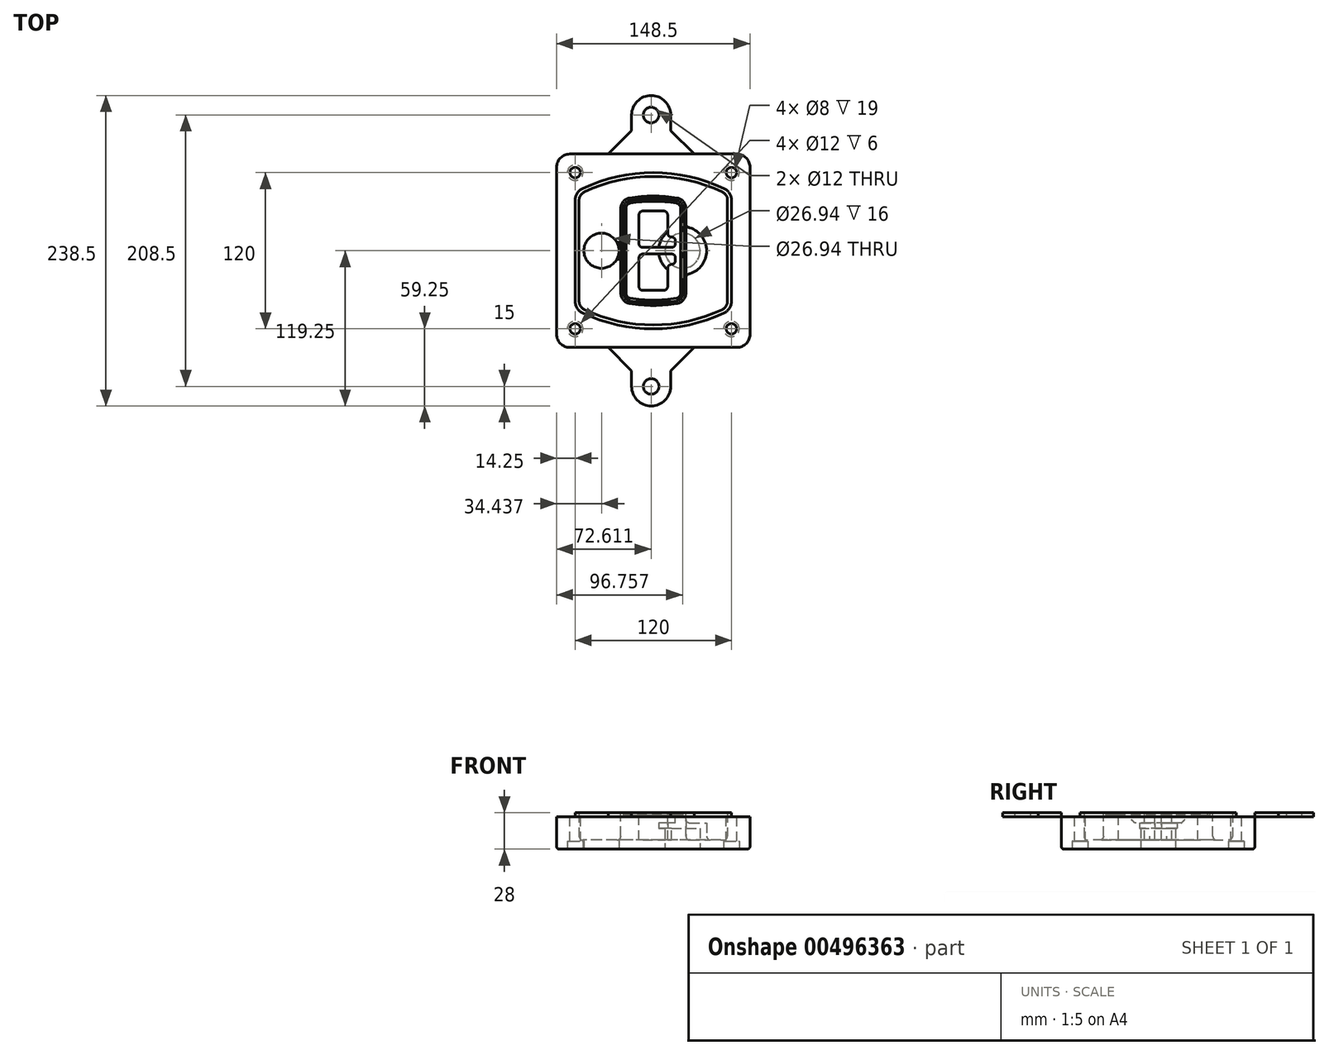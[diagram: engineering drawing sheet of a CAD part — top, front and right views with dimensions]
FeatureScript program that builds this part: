
annotation { "Feature Type Name" : "Feature", "Feature Type Description" : "" }
export const myFeature = defineFeature(function(context is Context, id is Id, definition is map)
    precondition{}
    {
        {
            var Q0;
            Q0=qCreatedBy(makeId("Top.planeOp"),FACE);
            var sketch = newSketch(context, id + "F0", { "sketchPlane" : qUnion([Q0])});
            skPoint(sketch, "E0.rect.middle", {"position": v(0, 0) * mm});
            skLineSegment(sketch, "E1.bottom", {"start": v(-64.25, -74.25) * mm, "end": v(64.25, -74.25) * mm});
            skLineSegment(sketch, "E1.top", {"start": v(-64.25, 74.25) * mm, "end": v(64.25, 74.25) * mm});
            skLineSegment(sketch, "E1.left", {"start": v(-74.25, -64.25) * mm, "end": v(-74.25, 64.25) * mm});
            skLineSegment(sketch, "E1.right", {"start": v(74.25, -64.25) * mm, "end": v(74.25, 64.25) * mm});
            skLineSegment(sketch, "E2", {"start": v(-74.25, 74.25) * mm, "end": v(74.25, -74.25) * mm, "construction": true});
            skLineSegment(sketch, "E3", {"start": v(74.25, 74.25) * mm, "end": v(-74.25, -74.25) * mm, "construction": true});
            skCircle(sketch, "E4", {"center": v(-60, 60) * mm, "radius": 4 * mm});
            skCircle(sketch, "E5", {"center": v(60, 60) * mm, "radius": 4 * mm});
            skCircle(sketch, "E6", {"center": v(60, -60) * mm, "radius": 4 * mm});
            skCircle(sketch, "E7", {"center": v(-60, -60) * mm, "radius": 4 * mm});
            skLineSegment(sketch, "E8", {"start": v(-60, 60) * mm, "end": v(60, 60) * mm, "construction": true});
            skLineSegment(sketch, "E9", {"start": v(60, 60) * mm, "end": v(60, -60) * mm, "construction": true});
            skLineSegment(sketch, "E10", {"start": v(60, -60) * mm, "end": v(-60, -60) * mm, "construction": true});
            skLineSegment(sketch, "E11", {"start": v(-60, -60) * mm, "end": v(-60, 60) * mm, "construction": true});
            skLineSegment(sketch, "E12", {"start": v(-60, 38.83) * mm, "end": v(-60, -38.83) * mm});
            skLineSegment(sketch, "E13", {"start": v(60, 38.83) * mm, "end": v(60, -38.83) * mm});
            skArc(sketch, "E14", {"start": v(54.26, 47.88) * mm, "mid": v(0, 60) * mm, "end": v(-54.26, 47.88) * mm});
            skArc(sketch, "E15", {"start": v(-54.26, -47.88) * mm, "mid": v(0, -60) * mm, "end": v(54.26, -47.88) * mm});
            skLineSegment(sketch, "E16", {"start": v(-60, 0) * mm, "end": v(60, 0) * mm, "construction": true});
            skPoint(sketch, "E17.visualSharp", {"position": v(-60, -45) * mm});
            skArc(sketch, "E17.filletArc", {"start": v(-60, -38.83) * mm, "mid": v(-58.44, -44.2) * mm, "end": v(-54.26, -47.88) * mm});
            skPoint(sketch, "E18.visualSharp", {"position": v(-60, 45) * mm});
            skArc(sketch, "E18.filletArc", {"start": v(-54.26, 47.88) * mm, "mid": v(-58.44, 44.2) * mm, "end": v(-60, 38.83) * mm});
            skPoint(sketch, "E19.visualSharp", {"position": v(60, 45) * mm});
            skArc(sketch, "E19.filletArc", {"start": v(60, 38.83) * mm, "mid": v(58.44, 44.2) * mm, "end": v(54.26, 47.88) * mm});
            skPoint(sketch, "E20.visualSharp", {"position": v(60, -45) * mm});
            skArc(sketch, "E20.filletArc", {"start": v(54.26, -47.88) * mm, "mid": v(58.44, -44.2) * mm, "end": v(60, -38.83) * mm});
            skPoint(sketch, "E21.visualSharp", {"position": v(-74.25, 74.25) * mm});
            skArc(sketch, "E21.filletArc", {"start": v(-64.25, 74.25) * mm, "mid": v(-71.32, 71.32) * mm, "end": v(-74.25, 64.25) * mm});
            skPoint(sketch, "E22.visualSharp", {"position": v(74.25, 74.25) * mm});
            skArc(sketch, "E22.filletArc", {"start": v(74.25, 64.25) * mm, "mid": v(71.32, 71.32) * mm, "end": v(64.25, 74.25) * mm});
            skPoint(sketch, "E23.visualSharp", {"position": v(74.25, -74.25) * mm});
            skArc(sketch, "E23.filletArc", {"start": v(64.25, -74.25) * mm, "mid": v(71.32, -71.32) * mm, "end": v(74.25, -64.25) * mm});
            skPoint(sketch, "E24.visualSharp", {"position": v(-74.25, -74.25) * mm});
            skArc(sketch, "E24.filletArc", {"start": v(-74.25, -64.25) * mm, "mid": v(-71.32, -71.32) * mm, "end": v(-64.25, -74.25) * mm});
            skArc(sketch, "E25.0", {"start": v(57, 38.83) * mm, "mid": v(55.9, 42.58) * mm, "end": v(52.98, 45.17) * mm});
            skLineSegment(sketch, "E25.1", {"start": v(57, 38.83) * mm, "end": v(57, -38.83) * mm});
            skArc(sketch, "E25.2", {"start": v(52.98, -45.17) * mm, "mid": v(55.9, -42.58) * mm, "end": v(57, -38.83) * mm});
            skArc(sketch, "E25.3", {"start": v(-52.98, -45.17) * mm, "mid": v(0, -57) * mm, "end": v(52.98, -45.17) * mm});
            skArc(sketch, "E25.4", {"start": v(-57, -38.83) * mm, "mid": v(-55.9, -42.58) * mm, "end": v(-52.98, -45.17) * mm});
            skArc(sketch, "E25.5", {"start": v(52.98, 45.17) * mm, "mid": v(0, 57) * mm, "end": v(-52.98, 45.17) * mm});
            skLineSegment(sketch, "E25.6", {"start": v(-57, 38.83) * mm, "end": v(-57, -38.83) * mm});
            skArc(sketch, "E25.7", {"start": v(-52.98, 45.17) * mm, "mid": v(-55.9, 42.58) * mm, "end": v(-57, 38.83) * mm});
            skArc(sketch, "E26.0", {"start": v(-55.96, 51.5) * mm, "mid": v(-61.82, 46.33) * mm, "end": v(-64, 38.83) * mm});
            skArc(sketch, "E26.1", {"start": v(55.96, 51.5) * mm, "mid": v(0, 64) * mm, "end": v(-55.96, 51.5) * mm});
            skArc(sketch, "E26.2", {"start": v(64, 38.83) * mm, "mid": v(61.82, 46.33) * mm, "end": v(55.96, 51.5) * mm});
            skLineSegment(sketch, "E26.3", {"start": v(64, 38.83) * mm, "end": v(64, -38.83) * mm});
            skArc(sketch, "E26.4", {"start": v(55.96, -51.5) * mm, "mid": v(61.82, -46.33) * mm, "end": v(64, -38.83) * mm});
            skLineSegment(sketch, "E26.5", {"start": v(-64, 38.83) * mm, "end": v(-64, -38.83) * mm});
            skArc(sketch, "E26.6", {"start": v(-55.96, -51.5) * mm, "mid": v(0, -64) * mm, "end": v(55.96, -51.5) * mm});
            skArc(sketch, "E26.7", {"start": v(-64, -38.83) * mm, "mid": v(-61.82, -46.33) * mm, "end": v(-55.96, -51.5) * mm});
            skSolve(sketch);
        }
        {
            var Q0;
            Q0=makeQuery(id+"F0.imprint","IMPRINT",FACE,{"disambiguationData":[TD([[makeQuery(id+"F0.imprint","IMPRINT",EDGE,{"derivedFrom":sQuery(id+"F0.wireOp",EDGE,"E1.bottom")}),1.0]])]});
            var Q1;
            Q1=makeQuery(id+"F0.imprint","IMPRINT",FACE,{"disambiguationData":[TD([[makeQuery(id+"F0.imprint","IMPRINT",EDGE,{"derivedFrom":sQuery(id+"F0.wireOp",EDGE,"E12")}),1.0]])]});
            var Q2;
            Q2=makeQuery(id+"F0.imprint","IMPRINT",FACE,{"disambiguationData":[TD([[makeQuery(id+"F0.imprint","IMPRINT",EDGE,{"derivedFrom":sQuery(id+"F0.wireOp",EDGE,"E25.0")}),1.0]])]});
            var Q3;
            Q3=makeQuery(id+"F0.imprint","IMPRINT",FACE,{"disambiguationData":[TD([[makeQuery(id+"F0.imprint","IMPRINT",EDGE,{"derivedFrom":sQuery(id+"F0.wireOp",EDGE,"E12")}),-1.0]])]});
            extrude(context, id + "F1", {"entities" : qUnion([Q0, Q1, Q2, Q3]), "oppositeDirection" : true, "depth" : 25 * mm});
        }
        {
            var Q0;
            Q0=makeQuery(id+"F0.imprint","IMPRINT",FACE,{"disambiguationData":[TD([[makeQuery(id+"F0.imprint","IMPRINT",EDGE,{"derivedFrom":sQuery(id+"F0.wireOp",EDGE,"E12")}),1.0]])]});
            extrude(context, id + "F2", {"entities" : qUnion([Q0]), "operationType" : NewBodyOperationType.ADD, "depth" : 3 * mm});
        }
        {
            var Q0;
            Q0=makeQuery(id+"F0.imprint","IMPRINT",FACE,{"disambiguationData":[TD([[makeQuery(id+"F0.imprint","IMPRINT",EDGE,{"derivedFrom":sQuery(id+"F0.wireOp",EDGE,"E25.0")}),1.0]])]});
            extrude(context, id + "F3", {"entities" : qUnion([Q0]), "operationType" : NewBodyOperationType.REMOVE, "oppositeDirection" : true, "depth" : 18 * mm});
        }
        {
            var Q0;
            Q0=makeQuery(id+"F2.opExtrude","CAP_FACE",FACE,{"disambiguationData":[OSD([sQuery(id+"F0.wireOp",EDGE,"E12"),sQuery(id+"F0.wireOp",EDGE,"E13"),sQuery(id+"F0.wireOp",EDGE,"E14"),sQuery(id+"F0.wireOp",EDGE,"E15"),sQuery(id+"F0.wireOp",EDGE,"E17.filletArc"),sQuery(id+"F0.wireOp",EDGE,"E18.filletArc"),sQuery(id+"F0.wireOp",EDGE,"E19.filletArc"),sQuery(id+"F0.wireOp",EDGE,"E20.filletArc"),sQuery(id+"F0.wireOp",EDGE,"E25.0"),sQuery(id+"F0.wireOp",EDGE,"E25.1"),sQuery(id+"F0.wireOp",EDGE,"E25.2"),sQuery(id+"F0.wireOp",EDGE,"E25.3"),sQuery(id+"F0.wireOp",EDGE,"E25.4"),sQuery(id+"F0.wireOp",EDGE,"E25.5"),sQuery(id+"F0.wireOp",EDGE,"E25.6"),sQuery(id+"F0.wireOp",EDGE,"E25.7")])],"isStart":false});
            var sketch = newSketch(context, id + "F4", { "sketchPlane" : qUnion([Q0])});
            skArc(sketch, "E27.0", {"start": v(-18.34, -40.45) * mm, "mid": v(0, -42) * mm, "end": v(18.34, -40.45) * mm});
            skArc(sketch, "E28.0", {"start": v(18.34, 40.45) * mm, "mid": v(0, 42) * mm, "end": v(-18.34, 40.45) * mm});
            skLineSegment(sketch, "E29", {"start": v(-25, 32.57) * mm, "end": v(-25, -32.57) * mm});
            skLineSegment(sketch, "E30", {"start": v(25, 32.57) * mm, "end": v(25, -32.57) * mm});
            skLineSegment(sketch, "E31", {"start": v(-25, 39.1) * mm, "end": v(25, 39.1) * mm, "construction": true});
            skLineSegment(sketch, "E32", {"start": v(-25, -39.1) * mm, "end": v(25, -39.1) * mm, "construction": true});
            skPoint(sketch, "E33.visualSharp", {"position": v(-25, 39.1) * mm});
            skArc(sketch, "E33.filletArc", {"start": v(-18.34, 40.45) * mm, "mid": v(-23.11, 37.73) * mm, "end": v(-25, 32.57) * mm});
            skPoint(sketch, "E34.visualSharp", {"position": v(25, 39.1) * mm});
            skArc(sketch, "E34.filletArc", {"start": v(25, 32.57) * mm, "mid": v(23.11, 37.73) * mm, "end": v(18.34, 40.45) * mm});
            skPoint(sketch, "E35.visualSharp", {"position": v(25, -39.1) * mm});
            skArc(sketch, "E35.filletArc", {"start": v(18.34, -40.45) * mm, "mid": v(23.11, -37.73) * mm, "end": v(25, -32.57) * mm});
            skPoint(sketch, "E36.visualSharp", {"position": v(-25, -39.1) * mm});
            skArc(sketch, "E36.filletArc", {"start": v(-25, -32.57) * mm, "mid": v(-23.11, -37.73) * mm, "end": v(-18.34, -40.45) * mm});
            skArc(sketch, "E37.0", {"start": v(52.98, 45.17) * mm, "mid": v(0, 57) * mm, "end": v(-52.98, 45.17) * mm});
            skArc(sketch, "E37.1", {"start": v(-52.98, 45.17) * mm, "mid": v(-55.9, 42.58) * mm, "end": v(-57, 38.83) * mm});
            skLineSegment(sketch, "E37.2", {"start": v(-57, 38.83) * mm, "end": v(-57, -38.83) * mm});
            skArc(sketch, "E37.3", {"start": v(-57, -38.83) * mm, "mid": v(-55.9, -42.58) * mm, "end": v(-52.98, -45.17) * mm});
            skArc(sketch, "E37.4", {"start": v(-52.98, -45.17) * mm, "mid": v(0, -57) * mm, "end": v(52.98, -45.17) * mm});
            skArc(sketch, "E37.5", {"start": v(52.98, -45.17) * mm, "mid": v(55.9, -42.58) * mm, "end": v(57, -38.83) * mm});
            skLineSegment(sketch, "E37.6", {"start": v(57, 38.83) * mm, "end": v(57, -38.83) * mm});
            skArc(sketch, "E37.7", {"start": v(57, 38.83) * mm, "mid": v(55.9, 42.58) * mm, "end": v(52.98, 45.17) * mm});
            skLineSegment(sketch, "E38.0", {"start": v(23, 32.57) * mm, "end": v(23, -32.57) * mm});
            skArc(sketch, "E38.1", {"start": v(18, -38.48) * mm, "mid": v(21.58, -36.44) * mm, "end": v(23, -32.57) * mm});
            skArc(sketch, "E38.2", {"start": v(-18, -38.48) * mm, "mid": v(0, -40) * mm, "end": v(18, -38.48) * mm});
            skArc(sketch, "E38.3", {"start": v(-23, -32.57) * mm, "mid": v(-21.58, -36.44) * mm, "end": v(-18, -38.48) * mm});
            skLineSegment(sketch, "E38.4", {"start": v(-23, 32.57) * mm, "end": v(-23, -32.57) * mm});
            skArc(sketch, "E38.5", {"start": v(23, 32.57) * mm, "mid": v(21.58, 36.44) * mm, "end": v(18, 38.48) * mm});
            skArc(sketch, "E38.6", {"start": v(-18, 38.48) * mm, "mid": v(-21.58, 36.44) * mm, "end": v(-23, 32.57) * mm});
            skArc(sketch, "E38.7", {"start": v(18, 38.48) * mm, "mid": v(0, 40) * mm, "end": v(-18, 38.48) * mm});
            skArc(sketch, "E39.0", {"start": v(21, 32.57) * mm, "mid": v(20.06, 35.15) * mm, "end": v(17.67, 36.5) * mm});
            skLineSegment(sketch, "E39.1", {"start": v(21, 32.57) * mm, "end": v(21, -32.57) * mm});
            skArc(sketch, "E39.2", {"start": v(17.67, -36.5) * mm, "mid": v(20.06, -35.15) * mm, "end": v(21, -32.57) * mm});
            skArc(sketch, "E39.3", {"start": v(-17.67, -36.5) * mm, "mid": v(0, -38) * mm, "end": v(17.67, -36.5) * mm});
            skArc(sketch, "E39.4", {"start": v(-21, -32.57) * mm, "mid": v(-20.06, -35.15) * mm, "end": v(-17.67, -36.5) * mm});
            skArc(sketch, "E39.5", {"start": v(17.67, 36.5) * mm, "mid": v(0, 38) * mm, "end": v(-17.67, 36.5) * mm});
            skLineSegment(sketch, "E39.6", {"start": v(-21, 32.57) * mm, "end": v(-21, -32.57) * mm});
            skArc(sketch, "E39.7", {"start": v(-17.67, 36.5) * mm, "mid": v(-20.06, 35.15) * mm, "end": v(-21, 32.57) * mm});
            skLineSegment(sketch, "E40", {"start": v(-25, 0) * mm, "end": v(25, 0) * mm, "construction": true});
            skLineSegment(sketch, "E41", {"start": v(-11, 5.5) * mm, "end": v(-11, 27.5) * mm});
            skLineSegment(sketch, "E42", {"start": v(-8, 30.5) * mm, "end": v(8, 30.5) * mm});
            skLineSegment(sketch, "E43", {"start": v(11, 27.5) * mm, "end": v(11, 13.5) * mm});
            skLineSegment(sketch, "E44", {"start": v(14, 10.5) * mm, "end": v(14, 10.5) * mm});
            skLineSegment(sketch, "E45", {"start": v(17, 7.5) * mm, "end": v(17, 5.5) * mm});
            skLineSegment(sketch, "E46", {"start": v(14, 2.5) * mm, "end": v(-8, 2.5) * mm});
            skPoint(sketch, "E47.visualSharp", {"position": v(-11, 30.5) * mm});
            skArc(sketch, "E47.filletArc", {"start": v(-8, 30.5) * mm, "mid": v(-10.12, 29.62) * mm, "end": v(-11, 27.5) * mm});
            skPoint(sketch, "E48.visualSharp", {"position": v(11, 30.5) * mm});
            skArc(sketch, "E48.filletArc", {"start": v(11, 27.5) * mm, "mid": v(10.12, 29.62) * mm, "end": v(8, 30.5) * mm});
            skPoint(sketch, "E49.visualSharp", {"position": v(11, 10.5) * mm});
            skArc(sketch, "E49.filletArc", {"start": v(11, 13.5) * mm, "mid": v(11.88, 11.38) * mm, "end": v(14, 10.5) * mm});
            skPoint(sketch, "E50.visualSharp", {"position": v(17, 10.5) * mm});
            skArc(sketch, "E50.filletArc", {"start": v(17, 7.5) * mm, "mid": v(16.12, 9.62) * mm, "end": v(14, 10.5) * mm});
            skPoint(sketch, "E51.visualSharp", {"position": v(17, 2.5) * mm});
            skArc(sketch, "E51.filletArc", {"start": v(14, 2.5) * mm, "mid": v(16.12, 3.38) * mm, "end": v(17, 5.5) * mm});
            skPoint(sketch, "E52.visualSharp", {"position": v(-11, 2.5) * mm});
            skArc(sketch, "E52.filletArc", {"start": v(-11, 5.5) * mm, "mid": v(-10.12, 3.38) * mm, "end": v(-8, 2.5) * mm});
            skLineSegment(sketch, "E53.0.MirrorCS", {"start": v(14, -2.5) * mm, "end": v(-8, -2.5) * mm});
            skArc(sketch, "E54.0.MirrorCS", {"start": v(-11, -5.5) * mm, "mid": v(-10.12, -3.38) * mm, "end": v(-8, -2.5) * mm});
            skLineSegment(sketch, "E55.0.MirrorCS", {"start": v(-11, -5.5) * mm, "end": v(-11, -27.5) * mm});
            skArc(sketch, "E56.0.MirrorCS", {"start": v(-8, -30.5) * mm, "mid": v(-10.12, -29.62) * mm, "end": v(-11, -27.5) * mm});
            skLineSegment(sketch, "E57.0.MirrorCS", {"start": v(-8, -30.5) * mm, "end": v(8, -30.5) * mm});
            skArc(sketch, "E58.0.MirrorCS", {"start": v(11, -27.5) * mm, "mid": v(10.12, -29.62) * mm, "end": v(8, -30.5) * mm});
            skLineSegment(sketch, "E59.0.MirrorCS", {"start": v(11, -27.5) * mm, "end": v(11, -13.5) * mm});
            skArc(sketch, "E60.0.MirrorCS", {"start": v(11, -13.5) * mm, "mid": v(11.88, -11.38) * mm, "end": v(14, -10.5) * mm});
            skArc(sketch, "E61.0.MirrorCS", {"start": v(17, -7.5) * mm, "mid": v(16.12, -9.62) * mm, "end": v(14, -10.5) * mm});
            skLineSegment(sketch, "E62.0.MirrorCS", {"start": v(17, -7.5) * mm, "end": v(17, -5.5) * mm});
            skArc(sketch, "E63.0.MirrorCS", {"start": v(14, -2.5) * mm, "mid": v(16.12, -3.38) * mm, "end": v(17, -5.5) * mm});
            skSolve(sketch);
        }
        {
            var Q0;
            Q0=makeQuery(id+"F4.imprint","IMPRINT",FACE,{"disambiguationData":[TD([[makeQuery(id+"F4.imprint","IMPRINT",EDGE,{"derivedFrom":sQuery(id+"F4.wireOp",EDGE,"E27.0")}),1.0]])]});
            var Q1;
            Q1=makeQuery(id+"F4.imprint","IMPRINT",FACE,{"disambiguationData":[TD([[makeQuery(id+"F4.imprint","IMPRINT",EDGE,{"derivedFrom":sQuery(id+"F4.wireOp",EDGE,"E38.0")}),-1.0]])]});
            var Q2;
            Q2=makeQuery(id+"F4.imprint","IMPRINT",FACE,{"disambiguationData":[TD([[makeQuery(id+"F4.imprint","IMPRINT",EDGE,{"derivedFrom":sQuery(id+"F4.wireOp",EDGE,"E39.0")}),1.0]])]});
            extrude(context, id + "F5", {"entities" : qUnion([Q0, Q1, Q2]), "operationType" : NewBodyOperationType.ADD, "endBound" : BoundingType.UP_TO_NEXT, "oppositeDirection" : true, "depth" : 25 * mm});
        }
        {
            var Q0;
            Q0=makeQuery(id+"F4.imprint","IMPRINT",FACE,{"disambiguationData":[TD([[makeQuery(id+"F4.imprint","IMPRINT",EDGE,{"derivedFrom":sQuery(id+"F4.wireOp",EDGE,"E38.0")}),-1.0]])]});
            extrude(context, id + "F6", {"entities" : qUnion([Q0]), "operationType" : NewBodyOperationType.REMOVE, "oppositeDirection" : true, "depth" : 2 * mm});
        }
        {
            var Q0;
            Q0=makeQuery(id+"F1.opExtrude","CAP_FACE",FACE,{"disambiguationData":[OSD([sQuery(id+"F0.wireOp",EDGE,"E1.bottom"),sQuery(id+"F0.wireOp",EDGE,"E1.top"),sQuery(id+"F0.wireOp",EDGE,"E1.left"),sQuery(id+"F0.wireOp",EDGE,"E1.right"),sQuery(id+"F0.wireOp",EDGE,"E4"),sQuery(id+"F0.wireOp",EDGE,"E5"),sQuery(id+"F0.wireOp",EDGE,"E6"),sQuery(id+"F0.wireOp",EDGE,"E7"),sQuery(id+"F0.wireOp",EDGE,"E21.filletArc"),sQuery(id+"F0.wireOp",EDGE,"E22.filletArc"),sQuery(id+"F0.wireOp",EDGE,"E23.filletArc"),sQuery(id+"F0.wireOp",EDGE,"E24.filletArc")])],"isStart":false});
            var sketch = newSketch(context, id + "F7", { "sketchPlane" : qUnion([Q0])});
            skCircle(sketch, "E64", {"center": v(22.5, 0) * mm, "radius": 13.47 * mm});
            skCircle(sketch, "E65", {"center": v(-39.81, 0) * mm, "radius": 13.47 * mm});
            skLineSegment(sketch, "E66", {"start": v(74.25, 0) * mm, "end": v(-74.25, 0) * mm});
            skCircle(sketch, "E67", {"center": v(22.5, 0) * mm, "radius": 18.47 * mm});
            skCircle(sketch, "E68", {"center": v(60, -60) * mm, "radius": 6 * mm});
            skCircle(sketch, "E69", {"center": v(-60, -60) * mm, "radius": 6 * mm});
            skCircle(sketch, "E70", {"center": v(-60, 60) * mm, "radius": 6 * mm});
            skCircle(sketch, "E71", {"center": v(60, 60) * mm, "radius": 6 * mm});
            skSolve(sketch);
        }
        {
            var Q0;
            {var subQ1=sQuery(id+"F7.wireOp",EDGE,"E66");var subQ4=sQuery(id+"F7.wireOp",EDGE,"E64");var subQ6=makeQuery(id+"F7.imprint","INTERSECT",VERTEX,{"disambiguationData":[OD(0.0)],"derivedFrom":[subQ4,subQ1]});Q0=makeQuery(id+"F7.imprint","IMPRINT",FACE,{"disambiguationData":[TD([[makeQuery(id+"F7.imprint","IMPRINT",EDGE,{"disambiguationData":[TD([[subQ6,-1.0]])],"derivedFrom":subQ4}),-1.0]])]});}
            var Q1;
            {var subQ0=sQuery(id+"F7.wireOp",EDGE,"E66");var subQ1=sQuery(id+"F7.wireOp",EDGE,"E64");var subQ3=makeQuery(id+"F7.imprint","INTERSECT",VERTEX,{"disambiguationData":[OD(0.0)],"derivedFrom":[subQ1,subQ0]});Q1=makeQuery(id+"F7.imprint","IMPRINT",FACE,{"disambiguationData":[TD([[makeQuery(id+"F7.imprint","IMPRINT",EDGE,{"disambiguationData":[TD([[subQ3,-1.0]])],"derivedFrom":subQ1}),1.0]])]});}
            var Q2;
            {var subQ0=sQuery(id+"F7.wireOp",EDGE,"E66");var subQ1=sQuery(id+"F7.wireOp",EDGE,"E64");var subQ3=makeQuery(id+"F7.imprint","INTERSECT",VERTEX,{"disambiguationData":[OD(0.0)],"derivedFrom":[subQ1,subQ0]});Q2=makeQuery(id+"F7.imprint","IMPRINT",FACE,{"disambiguationData":[TD([[makeQuery(id+"F7.imprint","IMPRINT",EDGE,{"disambiguationData":[TD([[subQ3,1.0]])],"derivedFrom":subQ1}),1.0]])]});}
            var Q3;
            {var subQ1=sQuery(id+"F7.wireOp",EDGE,"E66");var subQ4=sQuery(id+"F7.wireOp",EDGE,"E64");var subQ6=makeQuery(id+"F7.imprint","INTERSECT",VERTEX,{"disambiguationData":[OD(0.0)],"derivedFrom":[subQ4,subQ1]});Q3=makeQuery(id+"F7.imprint","IMPRINT",FACE,{"disambiguationData":[TD([[makeQuery(id+"F7.imprint","IMPRINT",EDGE,{"disambiguationData":[TD([[subQ6,1.0]])],"derivedFrom":subQ4}),-1.0]])]});}
            extrude(context, id + "F8", {"entities" : qUnion([Q0, Q1, Q2, Q3]), "operationType" : NewBodyOperationType.ADD, "oppositeDirection" : true, "depth" : 20 * mm});
        }
        {
            var Q0;
            {var subQ0=sQuery(id+"F7.wireOp",EDGE,"E66");var subQ1=sQuery(id+"F7.wireOp",EDGE,"E64");var subQ3=makeQuery(id+"F7.imprint","INTERSECT",VERTEX,{"disambiguationData":[OD(0.0)],"derivedFrom":[subQ1,subQ0]});Q0=makeQuery(id+"F7.imprint","IMPRINT",FACE,{"disambiguationData":[TD([[makeQuery(id+"F7.imprint","IMPRINT",EDGE,{"disambiguationData":[TD([[subQ3,-1.0]])],"derivedFrom":subQ1}),1.0]])]});}
            var Q1;
            {var subQ0=sQuery(id+"F7.wireOp",EDGE,"E66");var subQ1=sQuery(id+"F7.wireOp",EDGE,"E64");var subQ3=makeQuery(id+"F7.imprint","INTERSECT",VERTEX,{"disambiguationData":[OD(0.0)],"derivedFrom":[subQ1,subQ0]});Q1=makeQuery(id+"F7.imprint","IMPRINT",FACE,{"disambiguationData":[TD([[makeQuery(id+"F7.imprint","IMPRINT",EDGE,{"disambiguationData":[TD([[subQ3,1.0]])],"derivedFrom":subQ1}),1.0]])]});}
            extrude(context, id + "F9", {"entities" : qUnion([Q0, Q1]), "operationType" : NewBodyOperationType.REMOVE, "oppositeDirection" : true, "depth" : 16 * mm});
        }
        {
            var Q0;
            {var subQ0=sQuery(id+"F7.wireOp",EDGE,"E66");var subQ1=sQuery(id+"F7.wireOp",EDGE,"E65");var subQ3=makeQuery(id+"F7.imprint","INTERSECT",VERTEX,{"disambiguationData":[OD(0.0)],"derivedFrom":[subQ1,subQ0]});Q0=makeQuery(id+"F7.imprint","IMPRINT",FACE,{"disambiguationData":[TD([[makeQuery(id+"F7.imprint","IMPRINT",EDGE,{"disambiguationData":[TD([[subQ3,-1.0]])],"derivedFrom":subQ1}),1.0]])]});}
            var Q1;
            {var subQ0=sQuery(id+"F7.wireOp",EDGE,"E66");var subQ1=sQuery(id+"F7.wireOp",EDGE,"E65");var subQ3=makeQuery(id+"F7.imprint","INTERSECT",VERTEX,{"disambiguationData":[OD(0.0)],"derivedFrom":[subQ1,subQ0]});Q1=makeQuery(id+"F7.imprint","IMPRINT",FACE,{"disambiguationData":[TD([[makeQuery(id+"F7.imprint","IMPRINT",EDGE,{"disambiguationData":[TD([[subQ3,1.0]])],"derivedFrom":subQ1}),1.0]])]});}
            extrude(context, id + "F10", {"entities" : qUnion([Q0, Q1]), "operationType" : NewBodyOperationType.REMOVE, "oppositeDirection" : true, "depth" : 25 * mm});
        }
        {
            var Q0;
            Q0=makeQuery(id+"F7.imprint","IMPRINT",FACE,{"disambiguationData":[TD([[makeQuery(id+"F7.imprint","IMPRINT",EDGE,{"derivedFrom":sQuery(id+"F7.wireOp",EDGE,"E68")}),1.0]])]});
            var Q1;
            Q1=makeQuery(id+"F7.imprint","IMPRINT",FACE,{"disambiguationData":[TD([[makeQuery(id+"F7.imprint","IMPRINT",EDGE,{"derivedFrom":makeQuery(id+"F1.opExtrude","CAP_EDGE",EDGE,{"disambiguationData":[OSD([sQuery(id+"F0.wireOp",EDGE,"E5")])],"isStart":false})}),-1.0]])]});
            var Q2;
            Q2=makeQuery(id+"F7.imprint","IMPRINT",FACE,{"disambiguationData":[TD([[makeQuery(id+"F7.imprint","IMPRINT",EDGE,{"derivedFrom":sQuery(id+"F7.wireOp",EDGE,"E69")}),1.0]])]});
            var Q3;
            Q3=makeQuery(id+"F7.imprint","IMPRINT",FACE,{"disambiguationData":[TD([[makeQuery(id+"F7.imprint","IMPRINT",EDGE,{"derivedFrom":makeQuery(id+"F1.opExtrude","CAP_EDGE",EDGE,{"disambiguationData":[OSD([sQuery(id+"F0.wireOp",EDGE,"E4")])],"isStart":false})}),-1.0]])]});
            var Q4;
            Q4=makeQuery(id+"F7.imprint","IMPRINT",FACE,{"disambiguationData":[TD([[makeQuery(id+"F7.imprint","IMPRINT",EDGE,{"derivedFrom":sQuery(id+"F7.wireOp",EDGE,"E70")}),1.0]])]});
            var Q5;
            Q5=makeQuery(id+"F7.imprint","IMPRINT",FACE,{"disambiguationData":[TD([[makeQuery(id+"F7.imprint","IMPRINT",EDGE,{"derivedFrom":makeQuery(id+"F1.opExtrude","CAP_EDGE",EDGE,{"disambiguationData":[OSD([sQuery(id+"F0.wireOp",EDGE,"E7")])],"isStart":false})}),-1.0]])]});
            var Q6;
            Q6=makeQuery(id+"F7.imprint","IMPRINT",FACE,{"disambiguationData":[TD([[makeQuery(id+"F7.imprint","IMPRINT",EDGE,{"derivedFrom":sQuery(id+"F7.wireOp",EDGE,"E71")}),1.0]])]});
            var Q7;
            Q7=makeQuery(id+"F7.imprint","IMPRINT",FACE,{"disambiguationData":[TD([[makeQuery(id+"F7.imprint","IMPRINT",EDGE,{"derivedFrom":makeQuery(id+"F1.opExtrude","CAP_EDGE",EDGE,{"disambiguationData":[OSD([sQuery(id+"F0.wireOp",EDGE,"E6")])],"isStart":false})}),-1.0]])]});
            extrude(context, id + "F11", {"entities" : qUnion([Q0, Q1, Q2, Q3, Q4, Q5, Q6, Q7]), "operationType" : NewBodyOperationType.REMOVE, "oppositeDirection" : true, "depth" : 6 * mm});
        }
        {
            var Q0;
            Q0=makeQuery(id+"F9.boolean.opBoolean","COPY",FACE,{"derivedFrom":makeQuery(id+"F9.opExtrude","CAP_FACE",FACE,{"disambiguationData":[OSD([sQuery(id+"F7.wireOp",EDGE,"E64")])],"isStart":false})});
            var sketch = newSketch(context, id + "F12", { "sketchPlane" : qUnion([Q0])});
            skArc(sketch, "E72.0", {"start": v(11, 14.45) * mm, "mid": v(6.45, 9.13) * mm, "end": v(4.2, 2.5) * mm});
            skArc(sketch, "E72.1", {"start": v(4.2, -2.5) * mm, "mid": v(6.45, -9.13) * mm, "end": v(11, -14.45) * mm});
            skLineSegment(sketch, "E73", {"start": v(4.2, -2.5) * mm, "end": v(14, -2.5) * mm});
            skLineSegment(sketch, "E74.0", {"start": v(14, 2.5) * mm, "end": v(4.2, 2.5) * mm});
            skArc(sketch, "E74.1", {"start": v(14, 2.5) * mm, "mid": v(16.12, 3.38) * mm, "end": v(17, 5.5) * mm});
            skLineSegment(sketch, "E74.2", {"start": v(17, 7.5) * mm, "end": v(17, 5.5) * mm});
            skArc(sketch, "E74.3", {"start": v(17, 7.5) * mm, "mid": v(16.12, 9.62) * mm, "end": v(14, 10.5) * mm});
            skArc(sketch, "E74.4", {"start": v(11, 13.5) * mm, "mid": v(11.88, 11.38) * mm, "end": v(14, 10.5) * mm});
            skLineSegment(sketch, "E74.5", {"start": v(11, 14.45) * mm, "end": v(11, 13.5) * mm});
            skLineSegment(sketch, "E74.7", {"start": v(14, -2.5) * mm, "end": v(4.2, -2.5) * mm});
            skArc(sketch, "E74.8", {"start": v(14, -2.5) * mm, "mid": v(16.12, -3.38) * mm, "end": v(17, -5.5) * mm});
            skLineSegment(sketch, "E74.9", {"start": v(17, -7.5) * mm, "end": v(17, -5.5) * mm});
            skArc(sketch, "E74.10", {"start": v(17, -7.5) * mm, "mid": v(16.12, -9.62) * mm, "end": v(14, -10.5) * mm});
            skArc(sketch, "E74.11", {"start": v(11, -13.5) * mm, "mid": v(11.88, -11.38) * mm, "end": v(14, -10.5) * mm});
            skLineSegment(sketch, "E74.12", {"start": v(11, -14.45) * mm, "end": v(11, -13.5) * mm});
            skPoint(sketch, "E75.orphan", {"position": v(11, -27.5) * mm});
            skPoint(sketch, "E76.orphan", {"position": v(-8, -2.5) * mm});
            skPoint(sketch, "E77.orphan", {"position": v(-8, 2.5) * mm});
            skPoint(sketch, "E78.orphan", {"position": v(11, 27.5) * mm});
            skSolve(sketch);
        }
        {
            var Q0;
            {var subQ7=sQuery(id+"F12.wireOp",EDGE,"E72.0");var subQ14=sQuery(id+"F12.wireOp",EDGE,"E72.1");var subQ16=sQuery(id+"F12.wireOp",EDGE,"E74.1");var subQ18=sQuery(id+"F12.wireOp",EDGE,"E74.8");Q0=qUnion([makeQuery(id+"F12.imprint","IMPRINT",FACE,{"disambiguationData":[TD([[makeQuery(id+"F12.imprint","IMPRINT",EDGE,{"derivedFrom":subQ7}),1.0]])]}),makeQuery(id+"F12.imprint","IMPRINT",FACE,{"disambiguationData":[TD([[makeQuery(id+"F12.imprint","IMPRINT",EDGE,{"derivedFrom":subQ14}),1.0]])]}),makeQuery(id+"F12.imprint","IMPRINT",FACE,{"disambiguationData":[TD([[makeQuery(id+"F12.imprint","IMPRINT",EDGE,{"derivedFrom":subQ16}),1.0]])]}),makeQuery(id+"F12.imprint","IMPRINT",FACE,{"disambiguationData":[TD([[makeQuery(id+"F12.imprint","IMPRINT",EDGE,{"derivedFrom":subQ18}),-1.0]])]})]);}
            var Q1;
            Q1=makeQuery(id+"F5.boolean.opBoolean","SPLIT",FACE,{"disambiguationData":[TD([makeQuery(id+"F5.opExtrude","SWEPT_FACE",FACE,{"disambiguationData":[OSD([sQuery(id+"F4.wireOp",EDGE,"E41")])]})])],"derivedFrom":makeQuery(id+"F3.boolean.opBoolean","COPY",FACE,{"derivedFrom":makeQuery(id+"F3.opExtrude","CAP_FACE",FACE,{"disambiguationData":[OSD([sQuery(id+"F0.wireOp",EDGE,"E25.0"),sQuery(id+"F0.wireOp",EDGE,"E25.1"),sQuery(id+"F0.wireOp",EDGE,"E25.2"),sQuery(id+"F0.wireOp",EDGE,"E25.3"),sQuery(id+"F0.wireOp",EDGE,"E25.4"),sQuery(id+"F0.wireOp",EDGE,"E25.5"),sQuery(id+"F0.wireOp",EDGE,"E25.6"),sQuery(id+"F0.wireOp",EDGE,"E25.7")])],"isStart":false})})});
            extrude(context, id + "F13", {"entities" : qUnion([Q0]), "operationType" : NewBodyOperationType.REMOVE, "endBound" : BoundingType.UP_TO_SURFACE, "endBoundEntityFace" : qUnion([Q1]), "depth" : 25 * mm});
        }
        {
            var Q0;
            Q0=makeQuery(id+"F3.boolean.opBoolean","COPY",EDGE,{"derivedFrom":makeQuery(id+"F3.opExtrude","CAP_EDGE",EDGE,{"disambiguationData":[OSD([sQuery(id+"F0.wireOp",EDGE,"E25.6")])],"isStart":false})});
            var Q1;
            Q1=makeQuery(id+"F8.boolean.opBoolean","INTERSECT",EDGE,{"derivedFrom":[makeQuery(id+"F5.opExtrude","SWEPT_FACE",FACE,{"disambiguationData":[OSD([sQuery(id+"F4.wireOp",EDGE,"E30")])]}),makeQuery(id+"F8.opExtrude","CAP_FACE",FACE,{"disambiguationData":[OSD([sQuery(id+"F7.wireOp",EDGE,"E67")])],"isStart":false})]});
            var Q2;
            Q2=makeQuery(id+"F8.boolean.opBoolean","INTERSECT",EDGE,{"disambiguationData":[OD(1.0)],"derivedFrom":[makeQuery(id+"F5.opExtrude","SWEPT_FACE",FACE,{"disambiguationData":[OSD([sQuery(id+"F4.wireOp",EDGE,"E30")])]}),makeQuery(id+"F8.opExtrude","SWEPT_FACE",FACE,{"disambiguationData":[OSD([sQuery(id+"F7.wireOp",EDGE,"E67")])]})]});
            var Q3;
            {var subQ0=sQuery(id+"F4.wireOp",EDGE,"E30");Q3=makeQuery(id+"F8.boolean.opBoolean","SPLIT",EDGE,{"disambiguationData":[TD([makeQuery(id+"F5.opExtrude","SWEPT_FACE",FACE,{"disambiguationData":[OSD([sQuery(id+"F4.wireOp",EDGE,"E35.filletArc")])]})])],"derivedFrom":makeQuery(id+"F5.opExtrude","CAP_EDGE",EDGE,{"disambiguationData":[OSD([subQ0])],"isStart":false})});}
            var Q4;
            {var subQ0=sQuery(id+"F0.wireOp",EDGE,"E25.7");var subQ1=sQuery(id+"F0.wireOp",EDGE,"E25.1");var subQ2=sQuery(id+"F0.wireOp",EDGE,"E25.6");var subQ3=sQuery(id+"F0.wireOp",EDGE,"E25.5");var subQ4=sQuery(id+"F0.wireOp",EDGE,"E25.4");var subQ5=sQuery(id+"F0.wireOp",EDGE,"E25.0");var subQ6=sQuery(id+"F0.wireOp",EDGE,"E25.2");var subQ7=sQuery(id+"F0.wireOp",EDGE,"E25.3");Q4=makeQuery(id+"F8.boolean.opBoolean","INTERSECT",EDGE,{"derivedFrom":[makeQuery(id+"F5.boolean.opBoolean","SPLIT",FACE,{"disambiguationData":[TD([makeQuery(id+"F2.opExtrude","SWEPT_FACE",FACE,{"disambiguationData":[OSD([subQ5])]})])],"derivedFrom":makeQuery(id+"F3.boolean.opBoolean","COPY",FACE,{"derivedFrom":makeQuery(id+"F3.opExtrude","CAP_FACE",FACE,{"disambiguationData":[OSD([subQ5,subQ1,subQ6,subQ7,subQ4,subQ3,subQ2,subQ0])],"isStart":false})})}),makeQuery(id+"F8.opExtrude","SWEPT_FACE",FACE,{"disambiguationData":[OSD([sQuery(id+"F7.wireOp",EDGE,"E67")])]})]});}
            var Q5;
            Q5=makeQuery(id+"F8.boolean.opBoolean","INTERSECT",EDGE,{"disambiguationData":[OD(0.0)],"derivedFrom":[makeQuery(id+"F5.opExtrude","SWEPT_FACE",FACE,{"disambiguationData":[OSD([sQuery(id+"F4.wireOp",EDGE,"E30")])]}),makeQuery(id+"F8.opExtrude","SWEPT_FACE",FACE,{"disambiguationData":[OSD([sQuery(id+"F7.wireOp",EDGE,"E67")])]})]});
            fillet(context, id + "F14", {"entities" : qUnion([Q0, Q1, Q2, Q3, Q4, Q5]), "radius" : 3 * mm, "tangentPropagation" : true, "allowEdgeOverflow" : false});
        }
        {
            var Q0;
            Q0=makeQuery(id+"F1.opExtrude","CAP_EDGE",EDGE,{"disambiguationData":[OSD([sQuery(id+"F0.wireOp",EDGE,"E1.bottom")])],"isStart":false});
            fillet(context, id + "F15", {"entities" : qUnion([Q0]), "radius" : 2 * mm, "tangentPropagation" : true, "allowEdgeOverflow" : false});
        }
        {
            var Q0;
            {var subQ0=sQuery(id+"F0.wireOp",EDGE,"E21.filletArc");var subQ1=sQuery(id+"F0.wireOp",EDGE,"E7");var subQ2=sQuery(id+"F0.wireOp",EDGE,"E6");var subQ3=sQuery(id+"F0.wireOp",EDGE,"E5");var subQ4=sQuery(id+"F0.wireOp",EDGE,"E4");var subQ5=sQuery(id+"F0.wireOp",EDGE,"E22.filletArc");var subQ6=sQuery(id+"F0.wireOp",EDGE,"E1.bottom");var subQ7=sQuery(id+"F0.wireOp",EDGE,"E1.right");var subQ8=sQuery(id+"F0.wireOp",EDGE,"E1.top");var subQ9=sQuery(id+"F0.wireOp",EDGE,"E1.left");var subQ10=sQuery(id+"F0.wireOp",EDGE,"E23.filletArc");var subQ11=sQuery(id+"F0.wireOp",EDGE,"E24.filletArc");Q0=makeQuery(id+"F2.boolean.opBoolean","SPLIT",FACE,{"disambiguationData":[TD([makeQuery(id+"F1.opExtrude","SWEPT_FACE",FACE,{"disambiguationData":[OSD([subQ6])]})])],"derivedFrom":makeQuery(id+"F1.opExtrude","CAP_FACE",FACE,{"disambiguationData":[OSD([subQ6,subQ8,subQ9,subQ7,subQ4,subQ3,subQ2,subQ1,subQ0,subQ5,subQ10,subQ11])],"isStart":true})});}
            var sketch = newSketch(context, id + "F16", { "sketchPlane" : qUnion([Q0])});
            skLineSegment(sketch, "E79", {"start": v(-34.64, 74.25) * mm, "end": v(-16.64, 92.25) * mm});
            skLineSegment(sketch, "E80", {"start": v(31.36, 74.25) * mm, "end": v(13.36, 92.25) * mm});
            skLineSegment(sketch, "E81", {"start": v(13.36, 92.25) * mm, "end": v(13.36, 104.25) * mm});
            skLineSegment(sketch, "E82", {"start": v(-16.64, 92.25) * mm, "end": v(-16.64, 104.25) * mm});
            skArc(sketch, "E83", {"start": v(13.36, 104.25) * mm, "mid": v(-1.64, 119.25) * mm, "end": v(-16.64, 104.25) * mm});
            skCircle(sketch, "E84", {"center": v(-1.64, 104.25) * mm, "radius": 6 * mm});
            skLineSegment(sketch, "E85", {"start": v(-74.25, 0) * mm, "end": v(74.25, 0) * mm, "construction": true});
            skLineSegment(sketch, "E86", {"start": v(-1.64, 104.25) * mm, "end": v(-1.64, 74.25) * mm, "construction": true});
            skPoint(sketch, "E86.endSnap0", {"position": v(0, 74.25) * mm});
            skLineSegment(sketch, "E87.MirrorCS", {"start": v(-34.64, -74.25) * mm, "end": v(-16.64, -92.25) * mm});
            skLineSegment(sketch, "E88.MirrorCS", {"start": v(-16.64, -92.25) * mm, "end": v(-16.64, -104.25) * mm});
            skArc(sketch, "E89.MirrorCS", {"start": v(13.36, -104.25) * mm, "mid": v(-1.64, -119.25) * mm, "end": v(-16.64, -104.25) * mm});
            skLineSegment(sketch, "E90.MirrorCS", {"start": v(13.36, -92.25) * mm, "end": v(13.36, -104.25) * mm});
            skLineSegment(sketch, "E91.MirrorCS", {"start": v(31.36, -74.25) * mm, "end": v(13.36, -92.25) * mm});
            skCircle(sketch, "E92.MirrorC", {"center": v(-1.64, -104.25) * mm, "radius": 6 * mm});
            skLineSegment(sketch, "E93.MirrorCS", {"start": v(-1.64, -104.25) * mm, "end": v(-1.64, -74.25) * mm, "construction": true});
            skSolve(sketch);
        }
        {
            var Q0;
            {var subQ0=sQuery(id+"F16.wireOp",EDGE,"E79");Q0=makeQuery(id+"F16.imprint","IMPRINT",FACE,{"disambiguationData":[TD([[makeQuery(id+"F16.imprint","IMPRINT",EDGE,{"derivedFrom":subQ0}),-1.0]])]});}
            var Q1;
            {var subQ0=sQuery(id+"F16.wireOp",EDGE,"E87.MirrorCS");Q1=makeQuery(id+"F16.imprint","IMPRINT",FACE,{"disambiguationData":[TD([[makeQuery(id+"F16.imprint","IMPRINT",EDGE,{"derivedFrom":subQ0}),1.0]])]});}
            var Q2;
            Q2=makeQuery(id+"F2.opExtrude","CAP_FACE",FACE,{"disambiguationData":[OSD([sQuery(id+"F0.wireOp",EDGE,"E12"),sQuery(id+"F0.wireOp",EDGE,"E13"),sQuery(id+"F0.wireOp",EDGE,"E14"),sQuery(id+"F0.wireOp",EDGE,"E15"),sQuery(id+"F0.wireOp",EDGE,"E17.filletArc"),sQuery(id+"F0.wireOp",EDGE,"E18.filletArc"),sQuery(id+"F0.wireOp",EDGE,"E19.filletArc"),sQuery(id+"F0.wireOp",EDGE,"E20.filletArc"),sQuery(id+"F0.wireOp",EDGE,"E25.0"),sQuery(id+"F0.wireOp",EDGE,"E25.1"),sQuery(id+"F0.wireOp",EDGE,"E25.2"),sQuery(id+"F0.wireOp",EDGE,"E25.3"),sQuery(id+"F0.wireOp",EDGE,"E25.4"),sQuery(id+"F0.wireOp",EDGE,"E25.5"),sQuery(id+"F0.wireOp",EDGE,"E25.6"),sQuery(id+"F0.wireOp",EDGE,"E25.7")])],"isStart":false});
            extrude(context, id + "F17", {"entities" : qUnion([Q0, Q1]), "endBound" : BoundingType.UP_TO_SURFACE, "endBoundEntityFace" : qUnion([Q2]), "depth" : 25 * mm});
        }
    });
